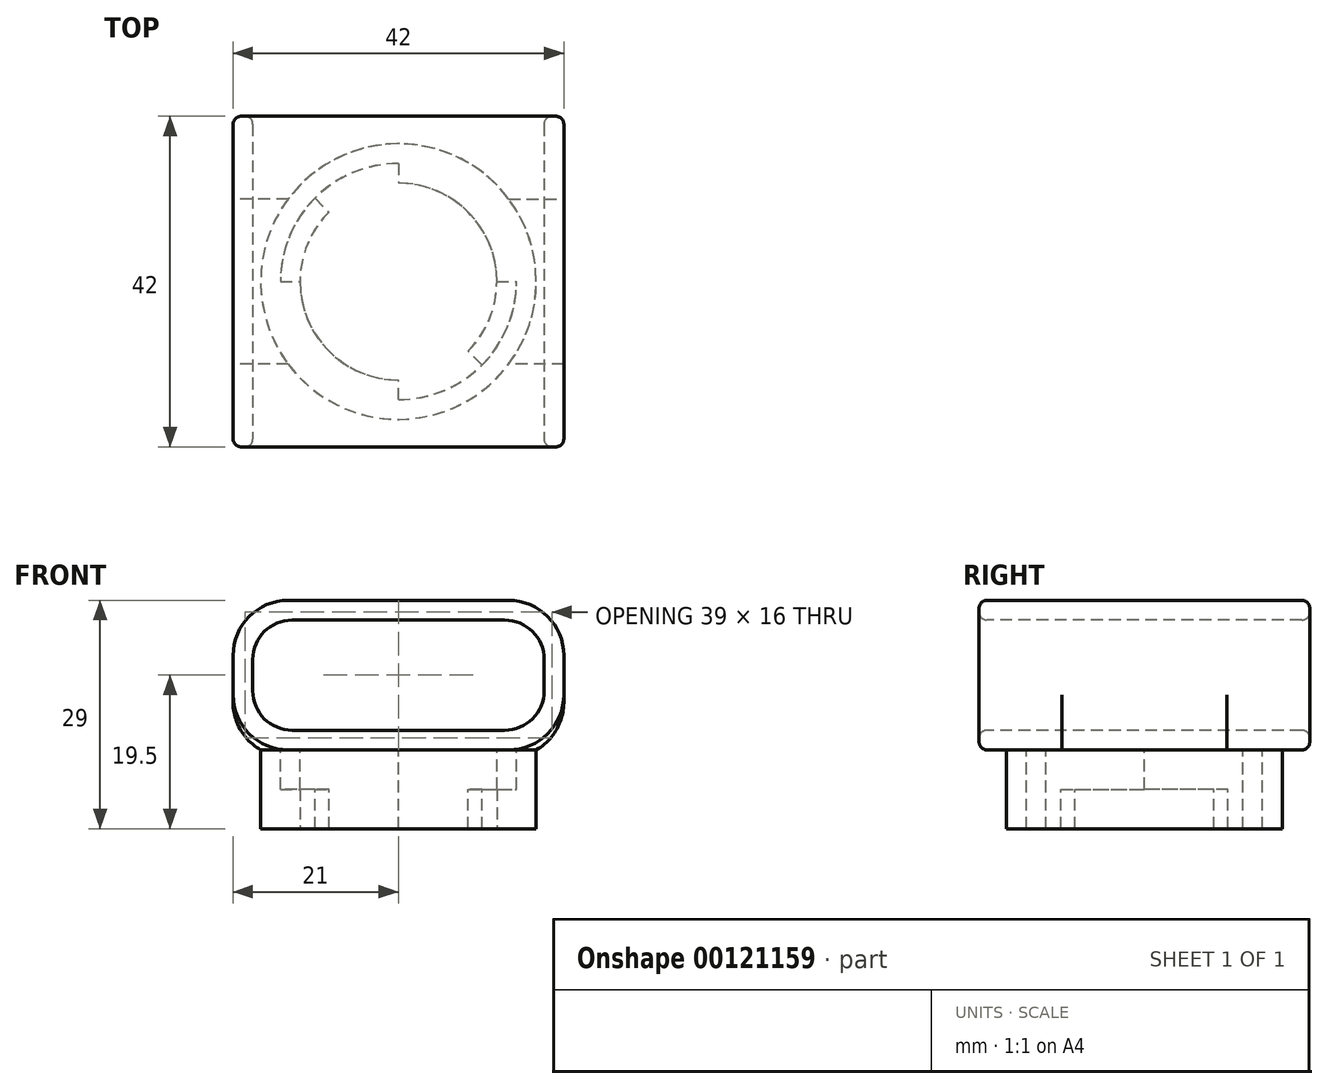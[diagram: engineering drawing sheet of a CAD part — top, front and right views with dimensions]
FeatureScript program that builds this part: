
annotation { "Feature Type Name" : "Feature", "Feature Type Description" : "" }
export const myFeature = defineFeature(function(context is Context, id is Id, definition is map)
    precondition{}
    {
        {
            var Q0;
            Q0=qCreatedBy(makeId("Top.planeOp"),FACE);
            var sketch = newSketch(context, id + "F0", { "sketchPlane" : qUnion([Q0])});
            skCircle(sketch, "E0", {"center": v(0, 0) * mm, "radius": 17.5 * mm});
            skCircle(sketch, "E1", {"center": v(0, 0) * mm, "radius": 12.5 * mm});
            skSolve(sketch);
        }
        {
            var Q0;
            Q0 = qSketchRegion(id + "F0", true);
            extrude(context, id + "F1", {"entities" : qUnion([Q0]), "depth" : 10 * mm});
        }
        {
            var Q0;
            Q0=makeQuery(id+"F1.opExtrude","CAP_FACE",FACE,{"disambiguationData":[OSD([sQuery(id+"F0.wireOp",EDGE,"E0"),sQuery(id+"F0.wireOp",EDGE,"E1")])],"isStart":false});
            var sketch = newSketch(context, id + "F2", { "sketchPlane" : qUnion([Q0])});
            skCircle(sketch, "E2", {"center": v(0, 0) * mm, "radius": 15 * mm});
            skLineSegment(sketch, "E3", {"start": v(-15, 0) * mm, "end": v(-12.5, 0) * mm});
            skLineSegment(sketch, "E4", {"start": v(12.5, 0) * mm, "end": v(15, 0) * mm});
            skLineSegment(sketch, "E5", {"start": v(-10.6, 10.6) * mm, "end": v(10.6, -10.6) * mm, "construction": true});
            skLineSegment(sketch, "E6", {"start": v(-10.6, 10.6) * mm, "end": v(-8.84, 8.84) * mm});
            skLineSegment(sketch, "E7", {"start": v(10.6, -10.6) * mm, "end": v(8.84, -8.84) * mm});
            skLineSegment(sketch, "E8", {"start": v(-10.6, -10.6) * mm, "end": v(10.6, 10.6) * mm, "construction": true});
            skLineSegment(sketch, "E9", {"start": v(0, 15) * mm, "end": v(0, 12.5) * mm});
            skLineSegment(sketch, "E10", {"start": v(0, -15) * mm, "end": v(0, -12.5) * mm});
            skSolve(sketch);
        }
        {
            var Q0;
            {var subQ0=sQuery(id+"F2.wireOp",EDGE,"E3");Q0=makeQuery(id+"F2.imprint","IMPRINT",FACE,{"disambiguationData":[TD([[makeQuery(id+"F2.imprint","IMPRINT",EDGE,{"derivedFrom":subQ0}),1.0]])]});}
            var Q1;
            {var subQ0=sQuery(id+"F2.wireOp",EDGE,"E4");Q1=makeQuery(id+"F2.imprint","IMPRINT",FACE,{"disambiguationData":[TD([[makeQuery(id+"F2.imprint","IMPRINT",EDGE,{"derivedFrom":subQ0}),-1.0]])]});}
            extrude(context, id + "F3", {"entities" : qUnion([Q0, Q1]), "operationType" : NewBodyOperationType.REMOVE, "oppositeDirection" : true, "depth" : 5 * mm});
        }
        {
            var Q0;
            {var subQ0=sQuery(id+"F2.wireOp",EDGE,"E6");Q0=makeQuery(id+"F2.imprint","IMPRINT",FACE,{"disambiguationData":[TD([[makeQuery(id+"F2.imprint","IMPRINT",EDGE,{"derivedFrom":subQ0}),1.0]])]});}
            var Q1;
            {var subQ0=sQuery(id+"F2.wireOp",EDGE,"E7");Q1=makeQuery(id+"F2.imprint","IMPRINT",FACE,{"disambiguationData":[TD([[makeQuery(id+"F2.imprint","IMPRINT",EDGE,{"derivedFrom":subQ0}),1.0]])]});}
            extrude(context, id + "F4", {"entities" : qUnion([Q0, Q1]), "operationType" : NewBodyOperationType.REMOVE, "endBound" : BoundingType.THROUGH_ALL, "oppositeDirection" : true, "depth" : 25 * mm});
        }
        {
            var Q0;
            Q0=makeQuery(id+"F1.opExtrude","CAP_FACE",FACE,{"disambiguationData":[OSD([sQuery(id+"F0.wireOp",EDGE,"E0"),sQuery(id+"F0.wireOp",EDGE,"E1")])],"isStart":false});
            var sketch = newSketch(context, id + "F5", { "sketchPlane" : qUnion([Q0])});
            skLineSegment(sketch, "E11.bottom", {"start": v(21, 21) * mm, "end": v(-21, 21) * mm});
            skLineSegment(sketch, "E11.top", {"start": v(21, -21) * mm, "end": v(-21, -21) * mm});
            skLineSegment(sketch, "E11.left", {"start": v(21, 21) * mm, "end": v(21, -21) * mm});
            skLineSegment(sketch, "E11.right", {"start": v(-21, 21) * mm, "end": v(-21, -21) * mm});
            skPoint(sketch, "E11.middle", {"position": v(0, 0) * mm});
            skSolve(sketch);
        }
        {
            var Q0;
            Q0 = qSketchRegion(id + "F5", true);
            extrude(context, id + "F6", {"entities" : qUnion([Q0]), "operationType" : NewBodyOperationType.ADD, "depth" : 19 * mm});
        }
        {
            var Q0;
            Q0=makeQuery(id+"F6.opExtrude","SWEPT_FACE",FACE,{"disambiguationData":[OSD([sQuery(id+"F5.wireOp",EDGE,"E11.top")])]});
            var sketch = newSketch(context, id + "F7", { "sketchPlane" : qUnion([Q0])});
            skLineSegment(sketch, "E12.bottom", {"start": v(13.5, 26.5) * mm, "end": v(-13.5, 26.5) * mm});
            skLineSegment(sketch, "E12.top", {"start": v(13.5, 12.5) * mm, "end": v(-13.5, 12.5) * mm});
            skLineSegment(sketch, "E12.left", {"start": v(18.5, 21.5) * mm, "end": v(18.5, 17.5) * mm});
            skLineSegment(sketch, "E12.right", {"start": v(-18.5, 21.5) * mm, "end": v(-18.5, 17.5) * mm});
            skPoint(sketch, "E12.middle", {"position": v(0, 19.5) * mm});
            skPoint(sketch, "E12.middle.positionSnap0", {"position": v(-21, 19.5) * mm});
            skPoint(sketch, "E12.middle.positionSnap1", {"position": v(0, 29) * mm});
            skPoint(sketch, "E12.centerSnap0", {"position": v(-21, 19.5) * mm});
            skPoint(sketch, "E12.centerSnap1", {"position": v(0, 29) * mm});
            skPoint(sketch, "E13.visualSharp", {"position": v(-18.5, 26.5) * mm});
            skArc(sketch, "E13.filletArc", {"start": v(-13.5, 26.5) * mm, "mid": v(-17.04, 25.04) * mm, "end": v(-18.5, 21.5) * mm});
            skPoint(sketch, "E14.visualSharp", {"position": v(-18.5, 12.5) * mm});
            skArc(sketch, "E14.filletArc", {"start": v(-18.5, 17.5) * mm, "mid": v(-17.04, 13.96) * mm, "end": v(-13.5, 12.5) * mm});
            skPoint(sketch, "E15.visualSharp", {"position": v(18.5, 26.5) * mm});
            skArc(sketch, "E15.filletArc", {"start": v(18.5, 21.5) * mm, "mid": v(17.04, 25.04) * mm, "end": v(13.5, 26.5) * mm});
            skPoint(sketch, "E16.visualSharp", {"position": v(18.5, 12.5) * mm});
            skArc(sketch, "E16.filletArc", {"start": v(13.5, 12.5) * mm, "mid": v(17.04, 13.96) * mm, "end": v(18.5, 17.5) * mm});
            skSolve(sketch);
        }
        {
            var Q0;
            Q0 = qSketchRegion(id + "F7", true);
            extrude(context, id + "F8", {"entities" : qUnion([Q0]), "operationType" : NewBodyOperationType.REMOVE, "endBound" : BoundingType.THROUGH_ALL, "oppositeDirection" : true, "depth" : 25 * mm});
        }
        {
            var Q0;
            Q0=makeQuery(id+"F6.opExtrude","CAP_EDGE",EDGE,{"disambiguationData":[OSD([sQuery(id+"F5.wireOp",EDGE,"E11.right")])],"isStart":true});
            var Q1;
            Q1=makeQuery(id+"F6.opExtrude","CAP_EDGE",EDGE,{"disambiguationData":[OSD([sQuery(id+"F5.wireOp",EDGE,"E11.right")])],"isStart":false});
            var Q2;
            Q2=makeQuery(id+"F6.opExtrude","CAP_EDGE",EDGE,{"disambiguationData":[OSD([sQuery(id+"F5.wireOp",EDGE,"E11.left")])],"isStart":false});
            var Q3;
            Q3=makeQuery(id+"F6.opExtrude","CAP_EDGE",EDGE,{"disambiguationData":[OSD([sQuery(id+"F5.wireOp",EDGE,"E11.left")])],"isStart":true});
            fillet(context, id + "F9", {"entities" : qUnion([Q0, Q1, Q2, Q3]), "radius" : 7 * mm, "tangentPropagation" : true, "allowEdgeOverflow" : false});
        }
        {
            var Q0;
            Q0=makeQuery(id+"F6.opExtrude","SWEPT_FACE",FACE,{"disambiguationData":[OSD([sQuery(id+"F5.wireOp",EDGE,"E11.top")])]});
            var Q1;
            Q1=makeQuery(id+"F6.opExtrude","SWEPT_FACE",FACE,{"disambiguationData":[OSD([sQuery(id+"F5.wireOp",EDGE,"E11.bottom")])]});
            fillet(context, id + "F10", {"entities" : qUnion([Q0, Q1]), "radius" : 1 * mm, "tangentPropagation" : true, "allowEdgeOverflow" : false});
        }
    });
